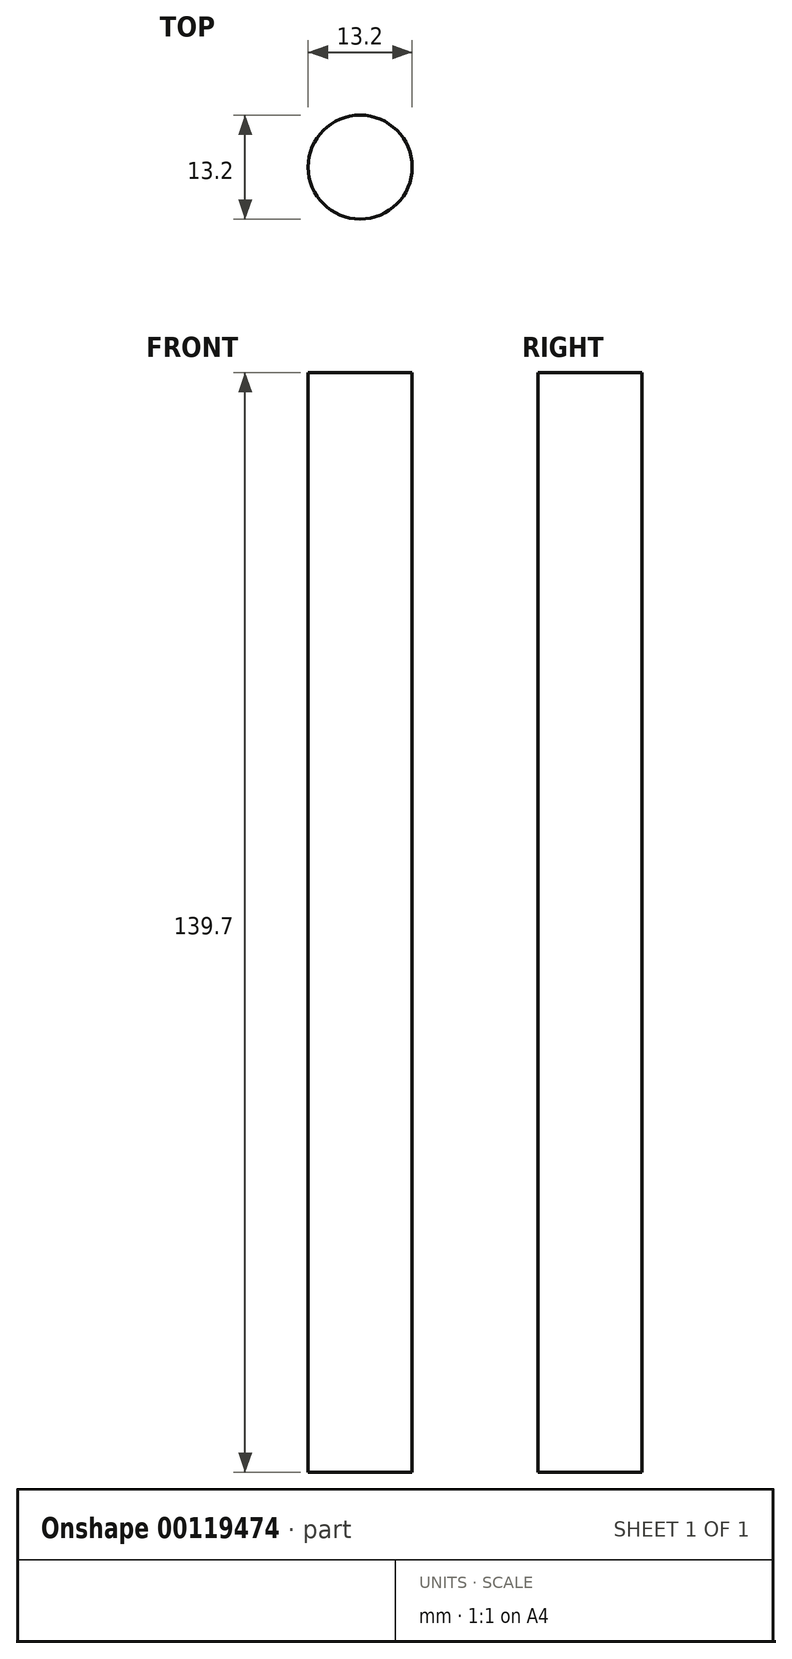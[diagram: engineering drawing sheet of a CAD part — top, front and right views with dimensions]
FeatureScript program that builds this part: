
annotation { "Feature Type Name" : "Feature", "Feature Type Description" : "" }
export const myFeature = defineFeature(function(context is Context, id is Id, definition is map)
    precondition{}
    {
        {
            var Q0;
            Q0=qCreatedBy(makeId("Top.planeOp"),FACE);
            var sketch = newSketch(context, id + "F0", { "sketchPlane" : qUnion([Q0])});
            skCircle(sketch, "E0", {"center": v(0, 0) * mm, "radius": 6.6 * mm});
            skSolve(sketch);
        }
        {
            var Q0;
            Q0=makeQuery(id+"F0.imprint","IMPRINT",FACE,{"disambiguationData":[TD([[makeQuery(id+"F0.imprint","IMPRINT",EDGE,{"derivedFrom":sQuery(id+"F0.wireOp",EDGE,"E0")}),1.0]])]});
            extrude(context, id + "F1", {"entities" : qUnion([Q0]), "depth" : 139.7 * mm});
        }
    });
